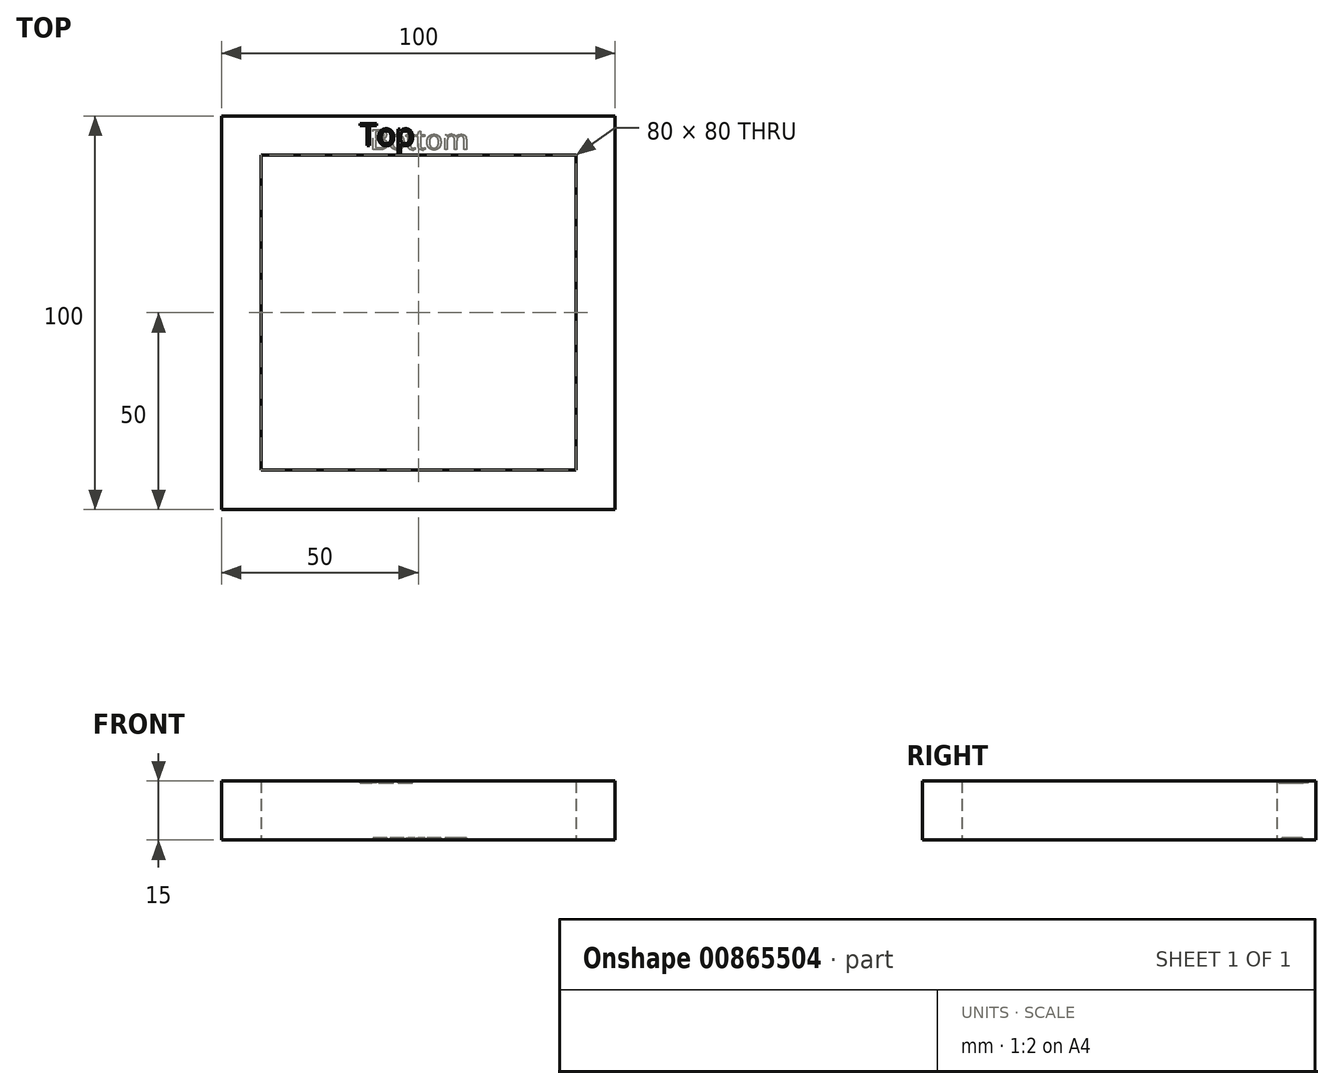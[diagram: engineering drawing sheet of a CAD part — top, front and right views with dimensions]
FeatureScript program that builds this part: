
annotation { "Feature Type Name" : "Feature", "Feature Type Description" : "" }
export const myFeature = defineFeature(function(context is Context, id is Id, definition is map)
    precondition{}
    {
        {
            var Q0;
            Q0=qCreatedBy(makeId("Top.planeOp"),FACE);
            var sketch = newSketch(context, id + "F0", { "sketchPlane" : qUnion([Q0])});
            skLineSegment(sketch, "E0.bottom", {"start": v(50, 50) * mm, "end": v(-50, 50) * mm});
            skLineSegment(sketch, "E0.top", {"start": v(50, -50) * mm, "end": v(-50, -50) * mm});
            skLineSegment(sketch, "E0.left", {"start": v(50, 50) * mm, "end": v(50, -50) * mm});
            skLineSegment(sketch, "E0.right", {"start": v(-50, 50) * mm, "end": v(-50, -50) * mm});
            skPoint(sketch, "E0.middle", {"position": v(0, 0) * mm});
            skLineSegment(sketch, "E1.bottom", {"start": v(40, 40) * mm, "end": v(-40, 40) * mm});
            skLineSegment(sketch, "E1.top", {"start": v(40, -40) * mm, "end": v(-40, -40) * mm});
            skLineSegment(sketch, "E1.left", {"start": v(40, 40) * mm, "end": v(40, -40) * mm});
            skLineSegment(sketch, "E1.right", {"start": v(-40, 40) * mm, "end": v(-40, -40) * mm});
            skSolve(sketch);
        }
        {
            var Q0;
            Q0 = qSketchRegion(id + "F0", true);
            extrude(context, id + "F1", {"entities" : qUnion([Q0]), "depth" : 15 * mm, "offsetDistance" : 25 * mm});
        }
        {
            var Q0;
            Q0=qCreatedBy(makeId("Top.planeOp"),FACE);
            cPlane(context, id + "F2", {"entities" : qUnion([Q0]), "cplaneType" : CPlaneType.OFFSET, "offset" : 15 * mm, "width" : 150 * mm, "height" : 150 * mm});
        }
        {
            var Q0;
            Q0=qCreatedBy(id+"F2.planeOp",FACE);
            var sketch = newSketch(context, id + "F3", { "sketchPlane" : qUnion([Q0])});
            skText(sketch, "E2", { "text": "Top", "fontName": "OpenSans-Regular.ttf"});
            const initialGuessF3  = {"E2": [-0.01487, 0.04247, 1, 0, 0.00562]};
            skSetInitialGuess(sketch, initialGuessF3);
            skSolve(sketch);
        }
        {
            var Q0;
            Q0 = qSketchRegion(id + "F3", true);
            extrude(context, id + "F4", {"entities" : qUnion([Q0]), "operationType" : NewBodyOperationType.REMOVE, "oppositeDirection" : true, "depth" : .5 * mm, "offsetDistance" : 25 * mm});
        }
        {
            var Q0;
            Q0=qCreatedBy(makeId("Top.planeOp"),FACE);
            var sketch = newSketch(context, id + "F5", { "sketchPlane" : qUnion([Q0])});
            skText(sketch, "E3", { "text": "Bottom", "fontName": "OpenSans-Regular.ttf"});
            const initialGuessF5  = {"E3": [-0.01222, 0.04141, 1, 0, 0.00515]};
            skSetInitialGuess(sketch, initialGuessF5);
            skSolve(sketch);
        }
        {
            var Q0;
            Q0 = qSketchRegion(id + "F5", true);
            extrude(context, id + "F6", {"entities" : qUnion([Q0]), "operationType" : NewBodyOperationType.REMOVE, "depth" : .5 * mm, "offsetDistance" : 25 * mm});
        }
    });
